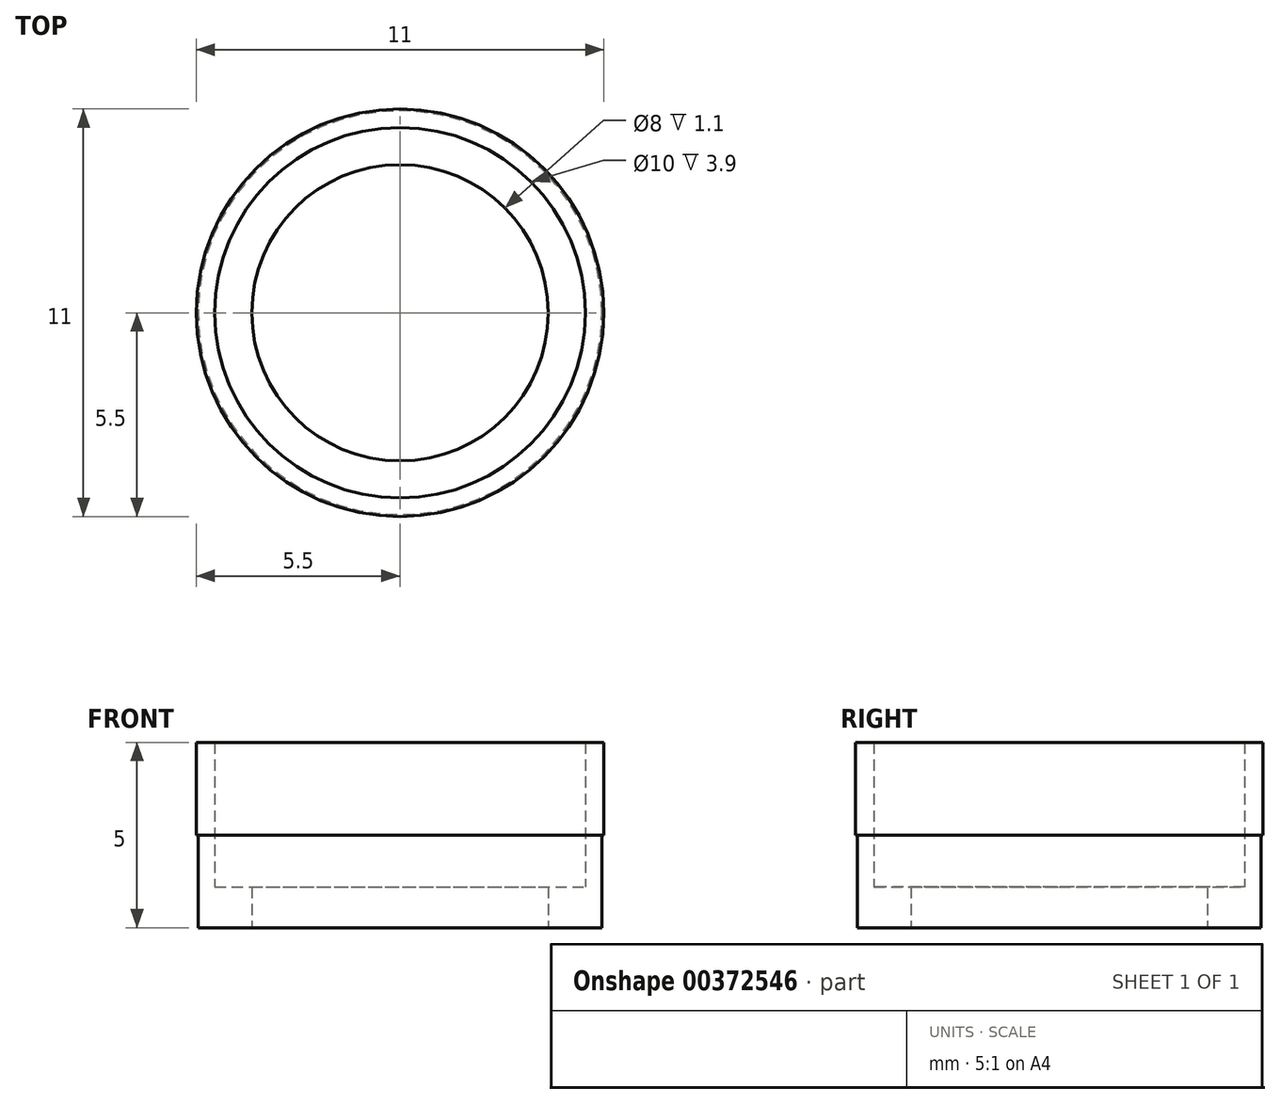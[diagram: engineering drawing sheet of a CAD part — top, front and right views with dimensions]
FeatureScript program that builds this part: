
annotation { "Feature Type Name" : "Feature", "Feature Type Description" : "" }
export const myFeature = defineFeature(function(context is Context, id is Id, definition is map)
    precondition{}
    {
        {
            var Q0;
            Q0=qCreatedBy(makeId("Front.planeOp"),FACE);
            var sketch = newSketch(context, id + "F0", { "sketchPlane" : qUnion([Q0])});
            skLineSegment(sketch, "E0", {"start": v(4, 0) * mm, "end": v(5.45, 0) * mm});
            skLineSegment(sketch, "E1", {"start": v(5.45, 0) * mm, "end": v(5.45, 2.5) * mm});
            skLineSegment(sketch, "E2", {"start": v(5.45, 2.5) * mm, "end": v(5.5, 2.5) * mm});
            skLineSegment(sketch, "E3", {"start": v(5.5, 2.5) * mm, "end": v(5.5, 5) * mm});
            skLineSegment(sketch, "E4", {"start": v(5.5, 5) * mm, "end": v(5, 5) * mm});
            skLineSegment(sketch, "E5", {"start": v(5, 5) * mm, "end": v(5, 1.1) * mm});
            skLineSegment(sketch, "E6", {"start": v(5, 1.1) * mm, "end": v(4, 1.1) * mm});
            skLineSegment(sketch, "E7", {"start": v(4, 1.1) * mm, "end": v(4, 0) * mm});
            skLineSegment(sketch, "E8", {"start": v(0, 0) * mm, "end": v(0, 5) * mm, "construction": true});
            skSolve(sketch);
        }
        {
            var Q0;
            Q0=makeQuery(id+"F0.imprint","IMPRINT",FACE,{"disambiguationData":[TD([[makeQuery(id+"F0.imprint","IMPRINT",EDGE,{"derivedFrom":sQuery(id+"F0.wireOp",EDGE,"E0")}),1.0]])]});
            var Q1;
            Q1=sQuery(id+"F0.wireOp",EDGE,"E8");
            revolve(context, id + "F1", {"entities" : qUnion([Q0]), "axis" : qUnion([Q1]), "revolveType" : RevolveType.FULL});
        }
    });
